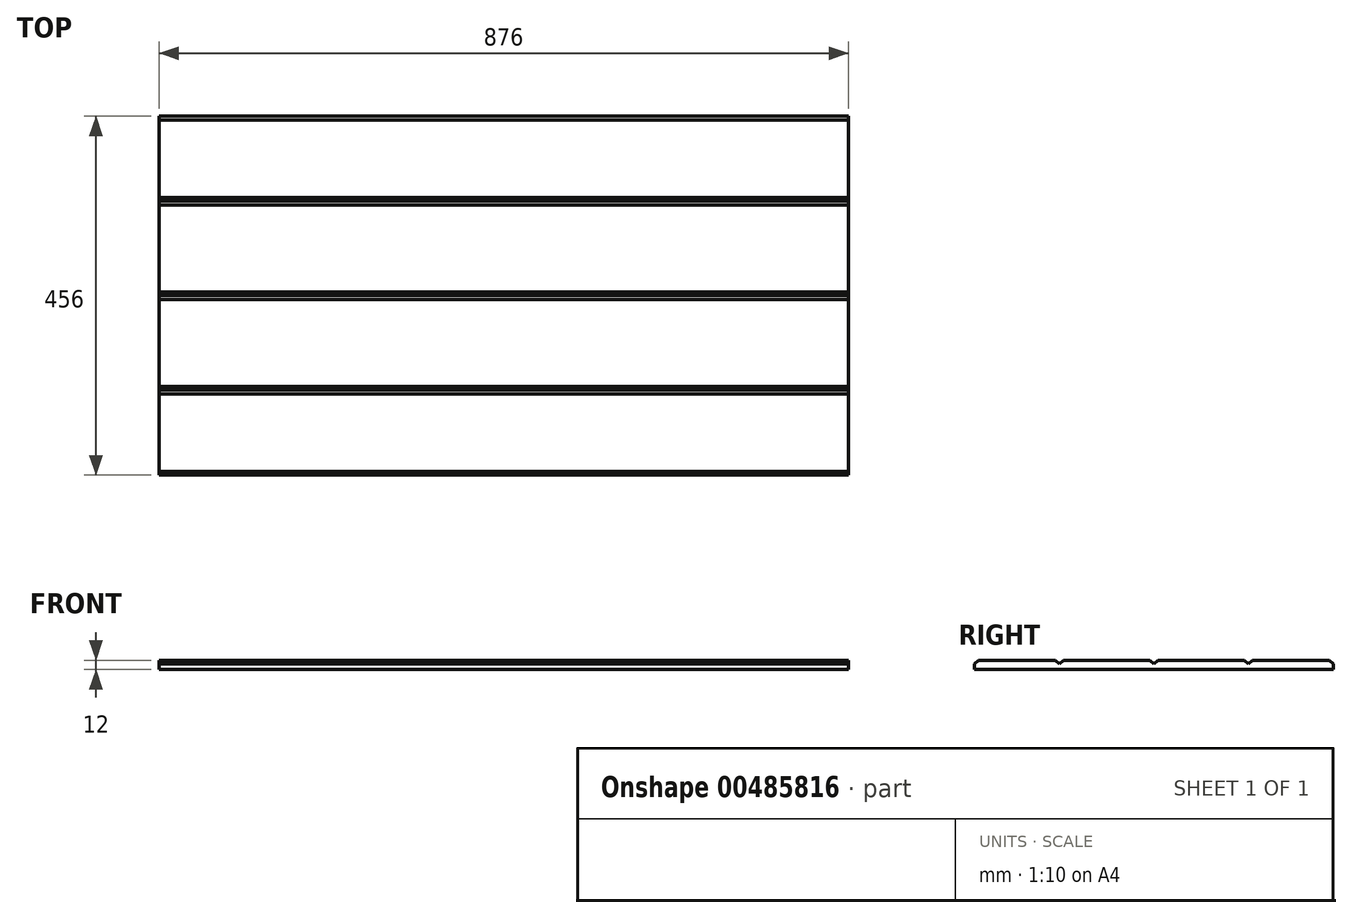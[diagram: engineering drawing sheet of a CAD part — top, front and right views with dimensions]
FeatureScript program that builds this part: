
annotation { "Feature Type Name" : "Feature", "Feature Type Description" : "" }
export const myFeature = defineFeature(function(context is Context, id is Id, definition is map)
    precondition{}
    {
        {
            var Q0;
            Q0=qCreatedBy(makeId("Top.planeOp"),FACE);
            var sketch = newSketch(context, id + "F0", { "sketchPlane" : qUnion([Q0])});
            skLineSegment(sketch, "E0.bottom", {"start": v(-324.23, 223.26) * mm, "end": v(551.77, 223.26) * mm});
            skLineSegment(sketch, "E0.top", {"start": v(-324.23, -232.74) * mm, "end": v(551.77, -232.74) * mm});
            skLineSegment(sketch, "E0.left", {"start": v(-324.23, 223.26) * mm, "end": v(-324.23, -232.74) * mm});
            skLineSegment(sketch, "E0.right", {"start": v(551.77, 223.26) * mm, "end": v(551.77, -232.74) * mm});
            skSolve(sketch);
        }
        {
            var Q0;
            Q0=makeQuery(id+"F0.imprint","IMPRINT",FACE,{"disambiguationData":[TD([[makeQuery(id+"F0.imprint","IMPRINT",EDGE,{"derivedFrom":sQuery(id+"F0.wireOp",EDGE,"E0.bottom")}),-1.0]])]});
            extrude(context, id + "F1", {"entities" : qUnion([Q0]), "depth" : 12 * mm});
        }
        {
            var Q0;
            Q0=makeQuery(id+"F1.opExtrude","SWEPT_FACE",FACE,{"disambiguationData":[OSD([sQuery(id+"F0.wireOp",EDGE,"E0.left")])]});
            var sketch = newSketch(context, id + "F2", { "sketchPlane" : qUnion([Q0])});
            skLineSegment(sketch, "E1", {"start": v(-223.26, 12) * mm, "end": v(-223.26, 7) * mm});
            skLineSegment(sketch, "E2", {"start": v(-223.26, 7) * mm, "end": v(-218.26, 12) * mm});
            skLineSegment(sketch, "E3", {"start": v(-218.26, 12) * mm, "end": v(-223.26, 12) * mm});
            skLineSegment(sketch, "E4", {"start": v(-223.26, 18.34) * mm, "end": v(-115.26, 18.34) * mm, "construction": true});
            skLineSegment(sketch, "E5", {"start": v(-115.26, 18.34) * mm, "end": v(4.74, 18.34) * mm, "construction": true});
            skLineSegment(sketch, "E6", {"start": v(4.74, 18.34) * mm, "end": v(124.74, 18.34) * mm, "construction": true});
            skLineSegment(sketch, "E7", {"start": v(124.74, 18.34) * mm, "end": v(232.74, 18.34) * mm, "construction": true});
            skLineSegment(sketch, "E8", {"start": v(232.74, 12) * mm, "end": v(227.74, 12) * mm});
            skLineSegment(sketch, "E9", {"start": v(227.74, 12) * mm, "end": v(232.74, 7) * mm});
            skLineSegment(sketch, "E10", {"start": v(232.74, 7) * mm, "end": v(232.74, 12) * mm});
            skLineSegment(sketch, "E11", {"start": v(124.74, 12) * mm, "end": v(119.74, 12) * mm});
            skLineSegment(sketch, "E12", {"start": v(119.74, 12) * mm, "end": v(124.74, 7) * mm});
            skLineSegment(sketch, "E13", {"start": v(124.74, 7) * mm, "end": v(129.74, 12) * mm});
            skLineSegment(sketch, "E14", {"start": v(129.74, 12) * mm, "end": v(124.74, 12) * mm});
            skLineSegment(sketch, "E15", {"start": v(4.74, 12) * mm, "end": v(-0.26, 12) * mm});
            skLineSegment(sketch, "E16", {"start": v(-0.26, 12) * mm, "end": v(4.74, 7) * mm});
            skLineSegment(sketch, "E17", {"start": v(4.74, 7) * mm, "end": v(9.74, 12) * mm});
            skLineSegment(sketch, "E18", {"start": v(9.74, 12) * mm, "end": v(4.74, 12) * mm});
            skLineSegment(sketch, "E19", {"start": v(-115.26, 12) * mm, "end": v(-120.26, 12) * mm});
            skLineSegment(sketch, "E20", {"start": v(-120.26, 12) * mm, "end": v(-115.26, 7) * mm});
            skLineSegment(sketch, "E21", {"start": v(-115.26, 7) * mm, "end": v(-110.26, 12) * mm});
            skLineSegment(sketch, "E22", {"start": v(-110.26, 12) * mm, "end": v(-115.26, 12) * mm});
            skSolve(sketch);
        }
        {
            var Q0;
            Q0 = qSketchRegion(id + "F2", true);
            extrude(context, id + "F3", {"entities" : qUnion([Q0]), "operationType" : NewBodyOperationType.REMOVE, "oppositeDirection" : true, "depth" : 900 * mm});
        }
    });
